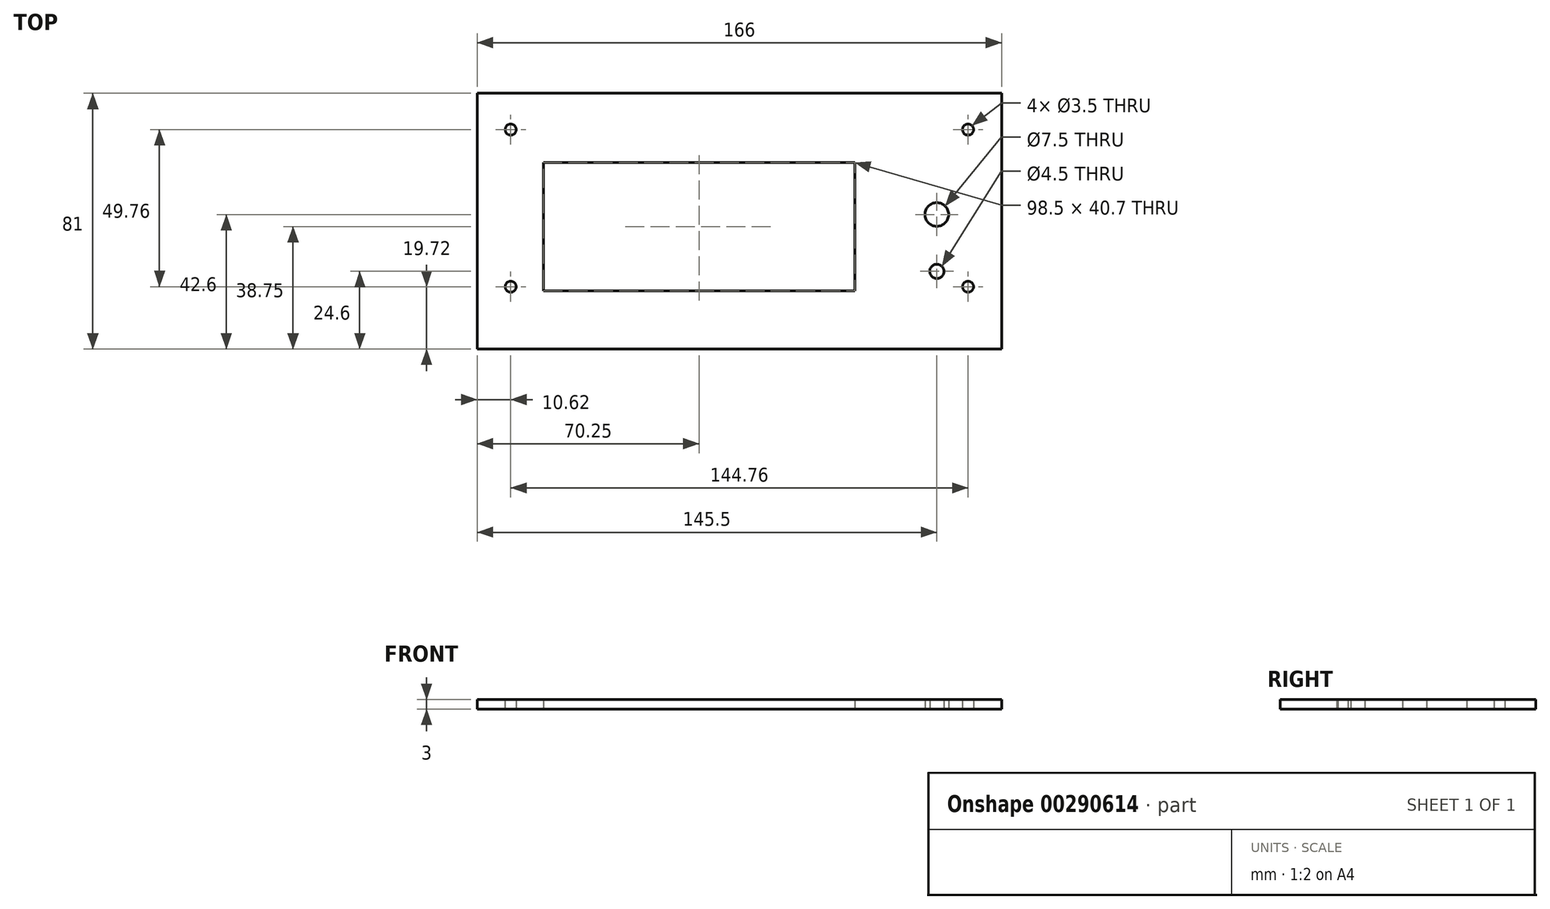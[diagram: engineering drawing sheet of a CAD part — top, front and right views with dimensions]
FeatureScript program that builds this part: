
annotation { "Feature Type Name" : "Feature", "Feature Type Description" : "" }
export const myFeature = defineFeature(function(context is Context, id is Id, definition is map)
    precondition{}
    {
        {
            var Q0;
            Q0=qCreatedBy(makeId("Top.planeOp"),FACE);
            var sketch = newSketch(context, id + "F0", { "sketchPlane" : qUnion([Q0])});
            skLineSegment(sketch, "E0.bottom", {"start": v(-83, 40.5) * mm, "end": v(83, 40.5) * mm});
            skLineSegment(sketch, "E0.top", {"start": v(-83, -40.5) * mm, "end": v(83, -40.5) * mm});
            skLineSegment(sketch, "E0.left", {"start": v(-83, 40.5) * mm, "end": v(-83, -40.5) * mm});
            skLineSegment(sketch, "E0.right", {"start": v(83, 40.5) * mm, "end": v(83, -40.5) * mm});
            skLineSegment(sketch, "E1", {"start": v(0, 40.5) * mm, "end": v(0, -40.5) * mm, "construction": true});
            skLineSegment(sketch, "E2.bottom", {"start": v(-75, 31.6) * mm, "end": v(75, 31.6) * mm});
            skLineSegment(sketch, "E2.top", {"start": v(-75, -31.6) * mm, "end": v(75, -31.6) * mm});
            skLineSegment(sketch, "E2.left", {"start": v(-75, 31.6) * mm, "end": v(-75, -31.6) * mm});
            skLineSegment(sketch, "E2.right", {"start": v(75, 31.6) * mm, "end": v(75, -31.6) * mm});
            skLineSegment(sketch, "E3.bottom", {"start": v(-62, 18.6) * mm, "end": v(36.5, 18.6) * mm});
            skLineSegment(sketch, "E3.top", {"start": v(-62, -22.1) * mm, "end": v(36.5, -22.1) * mm});
            skLineSegment(sketch, "E3.left", {"start": v(-62, 18.6) * mm, "end": v(-62, -22.1) * mm});
            skLineSegment(sketch, "E3.right", {"start": v(36.5, 18.6) * mm, "end": v(36.5, -22.1) * mm});
            skLineSegment(sketch, "E4.bottom", {"start": v(56, 8.1) * mm, "end": v(69, 8.1) * mm});
            skLineSegment(sketch, "E4.top", {"start": v(56, -3.9) * mm, "end": v(69, -3.9) * mm});
            skLineSegment(sketch, "E4.left", {"start": v(56, 8.1) * mm, "end": v(56, -3.9) * mm});
            skLineSegment(sketch, "E4.right", {"start": v(69, 8.1) * mm, "end": v(69, -3.9) * mm});
            skLineSegment(sketch, "E5", {"start": v(62.5, 8.1) * mm, "end": v(62.5, -3.9) * mm, "construction": true});
            skLineSegment(sketch, "E6", {"start": v(56, 2.1) * mm, "end": v(69, 2.1) * mm, "construction": true});
            skCircle(sketch, "E7", {"center": v(62.5, 2.1) * mm, "radius": 3.75 * mm});
            skLineSegment(sketch, "E8", {"start": v(75, -23.4) * mm, "end": v(-75, -23.4) * mm, "construction": true});
            skLineSegment(sketch, "E9.bottom", {"start": v(59.5, -12.9) * mm, "end": v(65.5, -12.9) * mm});
            skLineSegment(sketch, "E9.top", {"start": v(59.5, -18.9) * mm, "end": v(65.5, -18.9) * mm});
            skLineSegment(sketch, "E9.left", {"start": v(59.5, -12.9) * mm, "end": v(59.5, -18.9) * mm});
            skLineSegment(sketch, "E9.right", {"start": v(65.5, -12.9) * mm, "end": v(65.5, -18.9) * mm});
            skLineSegment(sketch, "E10", {"start": v(62.5, -12.9) * mm, "end": v(62.5, -18.9) * mm, "construction": true});
            skLineSegment(sketch, "E11", {"start": v(59.5, -15.9) * mm, "end": v(65.5, -15.9) * mm, "construction": true});
            skCircle(sketch, "E12", {"center": v(62.5, -15.9) * mm, "radius": 2.25 * mm});
            skCircle(sketch, "E13", {"center": v(-72.38, 28.98) * mm, "radius": 1.75 * mm});
            skCircle(sketch, "E14", {"center": v(72.38, 28.98) * mm, "radius": 1.75 * mm});
            skLineSegment(sketch, "E15", {"start": v(-72.38, 28.98) * mm, "end": v(-72.38, -23.4) * mm, "construction": true});
            skLineSegment(sketch, "E16", {"start": v(72.38, 28.98) * mm, "end": v(72.38, -23.4) * mm, "construction": true});
            skCircle(sketch, "E17", {"center": v(-72.38, -20.78) * mm, "radius": 1.75 * mm});
            skCircle(sketch, "E18", {"center": v(72.38, -20.78) * mm, "radius": 1.75 * mm});
            skSolve(sketch);
        }
        {
            var Q0;
            Q0=makeQuery(id+"F0.imprint","IMPRINT",FACE,{"disambiguationData":[TD([[makeQuery(id+"F0.imprint","IMPRINT",EDGE,{"derivedFrom":sQuery(id+"F0.wireOp",EDGE,"E2.bottom")}),-1.0]])]});
            var Q1;
            Q1=makeQuery(id+"F0.imprint","IMPRINT",FACE,{"disambiguationData":[TD([[makeQuery(id+"F0.imprint","IMPRINT",EDGE,{"derivedFrom":sQuery(id+"F0.wireOp",EDGE,"E0.bottom")}),-1.0]])]});
            var Q2;
            Q2=makeQuery(id+"F0.imprint","IMPRINT",FACE,{"disambiguationData":[TD([[makeQuery(id+"F0.imprint","IMPRINT",EDGE,{"derivedFrom":sQuery(id+"F0.wireOp",EDGE,"E4.bottom")}),-1.0]])]});
            var Q3;
            Q3=makeQuery(id+"F0.imprint","IMPRINT",FACE,{"disambiguationData":[TD([[makeQuery(id+"F0.imprint","IMPRINT",EDGE,{"derivedFrom":sQuery(id+"F0.wireOp",EDGE,"E9.bottom")}),-1.0]])]});
            extrude(context, id + "F1", {"entities" : qUnion([Q0, Q1, Q2, Q3]), "depth" : 3 * mm});
        }
    });
